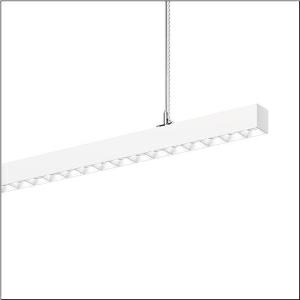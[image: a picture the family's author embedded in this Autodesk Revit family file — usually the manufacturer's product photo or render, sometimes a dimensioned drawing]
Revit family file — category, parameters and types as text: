
# Revit family: silica_r__21_51mx37da47wb_26de
name_source: partatom
category: Lighting Fixtures
units: mm (PartAtom-declared; Revit-internal decimal feet)

## family parameters
Cut with Voids When Loaded = No
Host = Face
Light Source = No
Part Type = Normal
Room Calculation Point = No
Round Connector Dimension = Use Diameter
Shared = No

## types (1)
- --- (1 x LED, 7300 lm, 44 W, 4000K)
    Apparent Load = 44 VA
    CIE Flux Codes = 71 92 99 59 100
    Color Rendering = 80
    Color Temperature = 4000K
    Default Elevation = 1800 mm
    Description = Silica® 21, office luminaire, primary light control with darklight reflector, of PMMA, white, CAT 2 (L<= 3000cd/m²), light emission: direct/indirect distribution, primary light characteristic: asymmetric, installation type: suspended mounting, LED, rated luminous flux: 7.300lm, luminous efficacy: 166lm/W, light colour: 840, colour temperature: 4000K, with terminal, 3+2-pole, max. 2.5mm², mains connection: 220..240V, AC, 50/60Hz, rated input power: 44W, luminaire housing, of aluminium, traffic white (RAL 9016), length: 1.204mm, width: 53mm, height: 53mm, protection rating (complete): IP20, insulation class (complete): insulation class I (protective earthing), certification: CE, permissible operating ambient temperature: 0..+35°C, standard: EN 50419, packaging unit: 1 piece
    Height = 53 mm
    Lamp = 1 x LED
    Lamp Light Flux = 7300 lm
    Lamp Power = 44 W
    Lamp count = 1
    Length = 1204 mm
    Luminous efficacy = 166 lm/W
    Manufacturer = Siteco
    ModVariant = No
    Model = 51MX37DA47WB
    Mounting Place = Ceiling
    Mounting Type = Pendant
    Number of Poles = 1
    OnlyDefault = Yes
    Power Factor = 1
    Product Name = Silica® 21
    Product group = office luminaire | ceiling pendant
    ProductGroupID = 902
    Protection Class = Protection class I
    Protection Degree = IP 20
    RLX_Detail_Level = 1
    RLX_Emergency_Light_Flux = 0 lm
    RLX_Emergency_Type = 0
    RLX_Emergency_Type_DB = No
    RlxData = <blob elided: 41625 chars, md5=bde96734>
    Socket = socket
    Standby Power = 0 W
    System Light Flux = 7300 lm
    System Power = 44 W
    Type Comments = factory setting: luminous flux: 100 % | dim-lin: 254 | 368 mA
    Type Image = l_1313634.jpg
    URL = http://relux.com
    VarID = @adj_068527
    Voltage = 0 V
    Weight = 0.00 kg
    Width = 53 mm

## geometry (parser evidence)
native form markers: Blend x4, Sweep x11
no freeform markers — native parametric forms only
